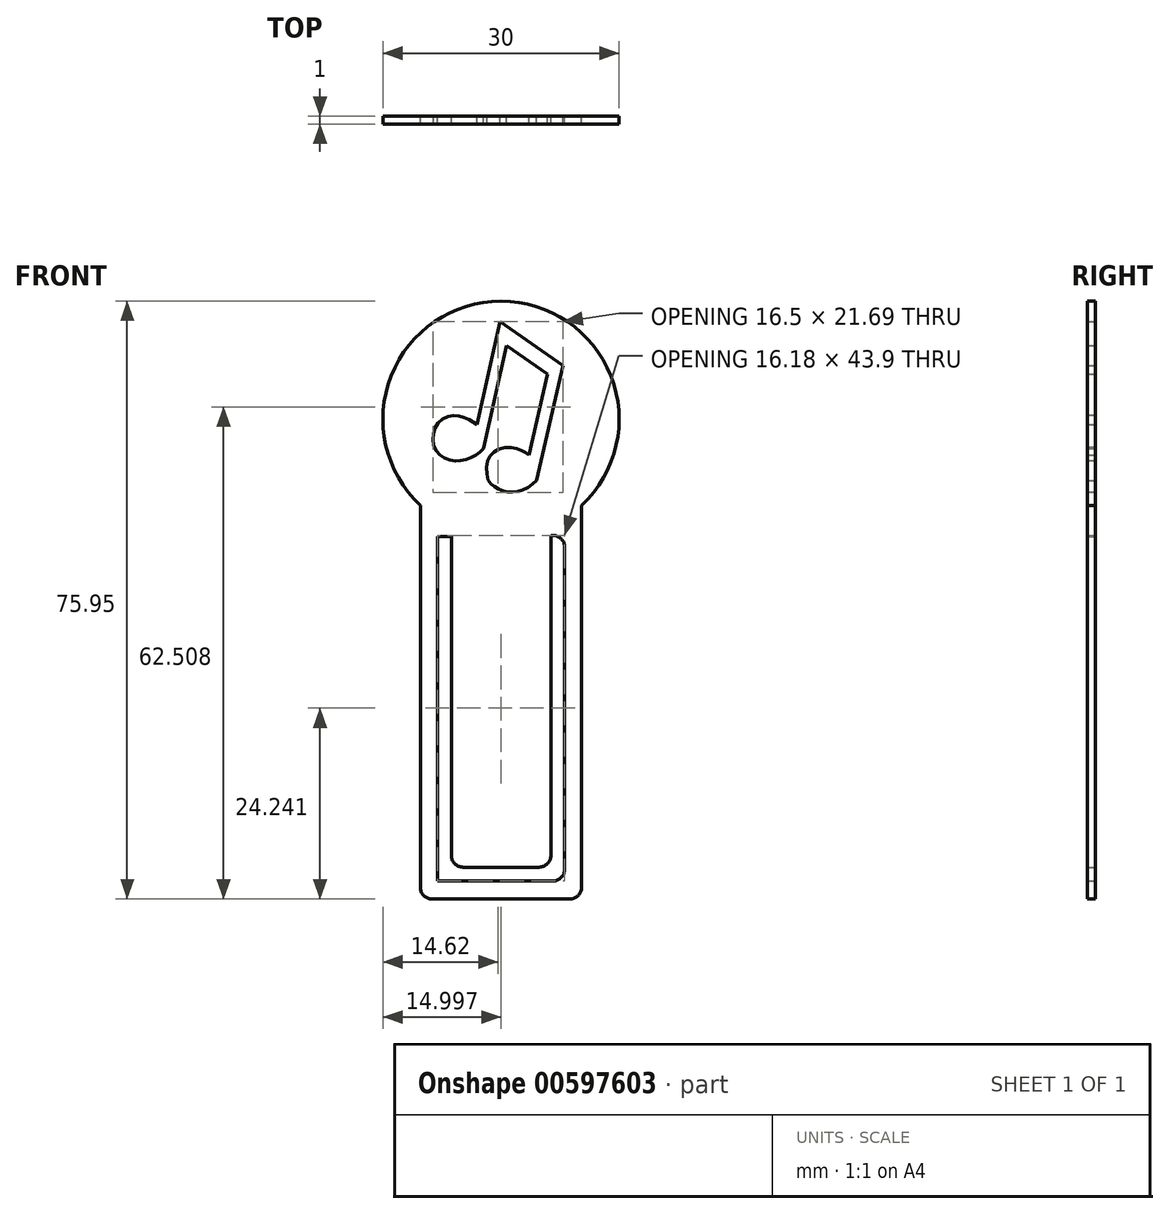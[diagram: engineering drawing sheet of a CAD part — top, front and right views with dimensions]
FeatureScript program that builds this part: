
annotation { "Feature Type Name" : "Feature", "Feature Type Description" : "" }
export const myFeature = defineFeature(function(context is Context, id is Id, definition is map)
    precondition{}
    {
        {
            var Q0;
            Q0=qCreatedBy(makeId("Front.planeOp"),FACE);
            var sketch = newSketch(context, id + "F0", { "sketchPlane" : qUnion([Q0])});
            skCircle(sketch, "E0", {"center": v(-22.83, 37.78) * mm, "radius": 15 * mm});
            skLineSegment(sketch, "E1.bottom", {"start": v(-33.08, 26.83) * mm, "end": v(-12.58, 26.83) * mm});
            skLineSegment(sketch, "E1.top", {"start": v(-33.08, -23.17) * mm, "end": v(-12.58, -23.17) * mm});
            skLineSegment(sketch, "E1.left", {"start": v(-33.08, 26.83) * mm, "end": v(-33.08, -23.17) * mm});
            skLineSegment(sketch, "E1.right", {"start": v(-12.58, 26.83) * mm, "end": v(-12.58, -23.17) * mm});
            skLineSegment(sketch, "E2.bottom", {"start": v(-66.52, 27.4) * mm, "end": v(-68.85, 27.4) * mm});
            skLineSegment(sketch, "E2.top", {"start": v(-66.52, 22.8) * mm, "end": v(-68.85, 22.8) * mm});
            skLineSegment(sketch, "E2.left", {"start": v(-68.85, 22.8) * mm, "end": v(-68.85, 27.4) * mm});
            skLineSegment(sketch, "E2.right", {"start": v(-66.52, 22.8) * mm, "end": v(-66.52, 27.4) * mm});
            skLineSegment(sketch, "E3.bottom", {"start": v(-66.52, 22.8) * mm, "end": v(-64.76, 22.8) * mm});
            skLineSegment(sketch, "E3.top", {"start": v(-66.52, 21.56) * mm, "end": v(-64.76, 21.56) * mm});
            skLineSegment(sketch, "E3.left", {"start": v(-66.52, 22.8) * mm, "end": v(-66.52, 21.56) * mm});
            skLineSegment(sketch, "E3.right", {"start": v(-64.76, 22.8) * mm, "end": v(-64.76, 21.56) * mm});
            skLineSegment(sketch, "E4.bottom", {"start": v(-30.92, 22.88) * mm, "end": v(-29.15, 22.88) * mm});
            skLineSegment(sketch, "E4.top", {"start": v(-30.92, -20.88) * mm, "end": v(-29.15, -20.88) * mm});
            skLineSegment(sketch, "E4.left", {"start": v(-30.92, 22.88) * mm, "end": v(-30.92, -20.88) * mm});
            skLineSegment(sketch, "E4.right", {"start": v(-29.15, 22.88) * mm, "end": v(-29.15, -20.88) * mm});
            skLineSegment(sketch, "E5.bottom", {"start": v(-30.92, -20.88) * mm, "end": v(-14.74, -20.88) * mm});
            skLineSegment(sketch, "E5.top", {"start": v(-30.92, -19.13) * mm, "end": v(-14.74, -19.13) * mm});
            skLineSegment(sketch, "E5.left", {"start": v(-30.92, -20.88) * mm, "end": v(-30.92, -19.13) * mm});
            skLineSegment(sketch, "E5.right", {"start": v(-14.74, -20.88) * mm, "end": v(-14.74, -19.13) * mm});
            skLineSegment(sketch, "E6.bottom", {"start": v(-14.74, -20.88) * mm, "end": v(-16.5, -20.88) * mm});
            skLineSegment(sketch, "E6.top", {"start": v(-14.74, 23.02) * mm, "end": v(-16.5, 23.02) * mm});
            skLineSegment(sketch, "E6.left", {"start": v(-14.74, -20.88) * mm, "end": v(-14.74, 23.02) * mm});
            skLineSegment(sketch, "E6.right", {"start": v(-16.5, -20.88) * mm, "end": v(-16.5, 23.02) * mm});
            skSolve(sketch);
        }
        {
            var Q0;
            {var subQ0=sQuery(id+"F0.wireOp",EDGE,"E1.bottom");var subQ1=sQuery(id+"F0.wireOp",EDGE,"E0");var subQ3=makeQuery(id+"F0.imprint","INTERSECT",VERTEX,{"derivedFrom":[subQ1,subQ0]});Q0=makeQuery(id+"F0.imprint","IMPRINT",FACE,{"disambiguationData":[TD([[makeQuery(id+"F0.imprint","IMPRINT",EDGE,{"disambiguationData":[TD([[subQ3,-1.0]])],"derivedFrom":subQ1}),1.0]])]});}
            var Q1;
            {var subQ0=sQuery(id+"F0.wireOp",EDGE,"E1.bottom");var subQ1=sQuery(id+"F0.wireOp",EDGE,"E0");var subQ3=makeQuery(id+"F0.imprint","INTERSECT",VERTEX,{"derivedFrom":[subQ1,subQ0]});Q1=makeQuery(id+"F0.imprint","IMPRINT",FACE,{"disambiguationData":[TD([[makeQuery(id+"F0.imprint","IMPRINT",EDGE,{"disambiguationData":[TD([[subQ3,1.0]])],"derivedFrom":subQ1}),1.0]])]});}
            var Q2;
            Q2=makeQuery(id+"F0.imprint","IMPRINT",FACE,{"disambiguationData":[TD([[makeQuery(id+"F0.imprint","IMPRINT",EDGE,{"derivedFrom":sQuery(id+"F0.wireOp",EDGE,"E1.top")}),1.0]])]});
            extrude(context, id + "F1", {"entities" : qUnion([Q0, Q1, Q2]), "depth" : 1 * mm, "offsetDistance" : 25 * mm});
        }
        {
            var Q0;
            Q0=makeQuery(id+"F1.opExtrude","SWEPT_EDGE",EDGE,{"disambiguationData":[OSD([sQuery(id+"F0.wireOp",EDGE,"E1.top"),sQuery(id+"F0.wireOp",EDGE,"E1.left")])]});
            var Q1;
            Q1=makeQuery(id+"F1.opExtrude","SWEPT_EDGE",EDGE,{"disambiguationData":[OSD([sQuery(id+"F0.wireOp",EDGE,"E4.right"),sQuery(id+"F0.wireOp",EDGE,"E5.top")])]});
            fillet(context, id + "F2", {"entities" : qUnion([Q0, Q1]), "radius" : 1.5 * mm, "tangentPropagation" : true, "allowEdgeOverflow" : false});
        }
        {
            var Q0;
            Q0=makeQuery(id+"F1.opExtrude","SWEPT_EDGE",EDGE,{"disambiguationData":[OSD([sQuery(id+"F0.wireOp",EDGE,"E1.top"),sQuery(id+"F0.wireOp",EDGE,"E1.right")])]});
            var Q1;
            Q1=makeQuery(id+"F1.opExtrude","SWEPT_EDGE",EDGE,{"disambiguationData":[OSD([sQuery(id+"F0.wireOp",EDGE,"E5.top"),sQuery(id+"F0.wireOp",EDGE,"E6.right")])]});
            fillet(context, id + "F3", {"entities" : qUnion([Q0, Q1]), "radius" : 1.5 * mm, "tangentPropagation" : true, "allowEdgeOverflow" : false});
        }
        {
            var Q0;
            Q0=makeQuery(id+"F1.opExtrude","SWEPT_EDGE",EDGE,{"disambiguationData":[OSD([sQuery(id+"F0.wireOp",EDGE,"E6.bottom"),sQuery(id+"F0.wireOp",EDGE,"E6.left")])]});
            fillet(context, id + "F4", {"entities" : qUnion([Q0]), "radius" : 1.5 * mm, "tangentPropagation" : true, "allowEdgeOverflow" : false});
        }
        {
            var Q0;
            Q0=makeQuery(id+"F1.opExtrude","SWEPT_EDGE",EDGE,{"disambiguationData":[OSD([sQuery(id+"F0.wireOp",EDGE,"E5.bottom"),sQuery(id+"F0.wireOp",EDGE,"E5.left")])]});
            fillet(context, id + "F5", {"entities" : qUnion([Q0]), "radius" : 1.5 * mm, "tangentPropagation" : true, "allowEdgeOverflow" : false});
        }
        {
            var Q0;
            Q0=qCreatedBy(makeId("Front.planeOp"),FACE);
            var sketch = newSketch(context, id + "F6", { "sketchPlane" : qUnion([Q0])});
            skLineSegment(sketch, "E7", {"start": v(-25.9, 37.12) * mm, "end": v(-22.93, 50.19) * mm});
            skLineSegment(sketch, "E8", {"start": v(-22.93, 50.19) * mm, "end": v(-14.96, 44.6) * mm});
            skLineSegment(sketch, "E9", {"start": v(-14.96, 44.6) * mm, "end": v(-18.3, 30) * mm});
            skFitSpline(sketch, "E10", {"points": [v(-18.3, 30) * mm, v(-19.71, 28.97) * mm, v(-21.3, 28.5) * mm, v(-22.41, 28.6) * mm, v(-23.67, 29.21) * mm, v(-24.44, 30) * mm, v(-24.59, 32.22) * mm, v(-23.64, 33.69) * mm, v(-21.83, 34.18) * mm, v(-20.17, 33.78) * mm, v(-19.26, 33.22) * mm], "startDerivative": vector(-12.5, -10.96) * mm, "endDerivative": vector(10.9, -7.71) * mm});
            skLineSegment(sketch, "E11", {"start": v(-19.26, 33.22) * mm, "end": v(-16.9, 43.49) * mm});
            skLineSegment(sketch, "E12", {"start": v(-16.9, 43.49) * mm, "end": v(-22.1, 47.13) * mm});
            skLineSegment(sketch, "E13", {"start": v(-22.1, 47.13) * mm, "end": v(-25.08, 34.06) * mm});
            skFitSpline(sketch, "E14", {"points": [v(-25.08, 34.06) * mm, v(-26, 33.23) * mm, v(-27.32, 32.68) * mm, v(-28.67, 32.5) * mm, v(-30.1, 32.9) * mm, v(-31.24, 34.06) * mm, v(-31.46, 35.68) * mm, v(-30.9, 37.21) * mm, v(-29.46, 38.17) * mm, v(-27.96, 38.1) * mm, v(-26.8, 37.64) * mm, v(-25.9, 37.12) * mm], "startDerivative": vector(-10.01, -10.6) * mm, "endDerivative": vector(11.16, -6.96) * mm});
            skLineSegment(sketch, "E15", {"start": v(-3.93, 42.96) * mm, "end": v(-3.6, 44.4) * mm});
            skLineSegment(sketch, "E16", {"start": v(-3.6, 44.4) * mm, "end": v(-4, 45.57) * mm});
            skLineSegment(sketch, "E17", {"start": v(-4, 45.57) * mm, "end": v(-7.12, 31.87) * mm});
            skLineSegment(sketch, "E18", {"start": v(-3.93, 42.96) * mm, "end": v(-7.12, 31.87) * mm});
            skSolve(sketch);
        }
        {
            var Q0;
            Q0 = qSketchRegion(id + "F6", true);
            extrude(context, id + "F7", {"entities" : qUnion([Q0]), "operationType" : NewBodyOperationType.REMOVE, "depth" : 2 * mm, "offsetDistance" : 25 * mm, "hasSecondDirection" : true, "secondDirectionOppositeDirection" : true, "secondDirectionDepth" : 2 * mm});
        }
    });
